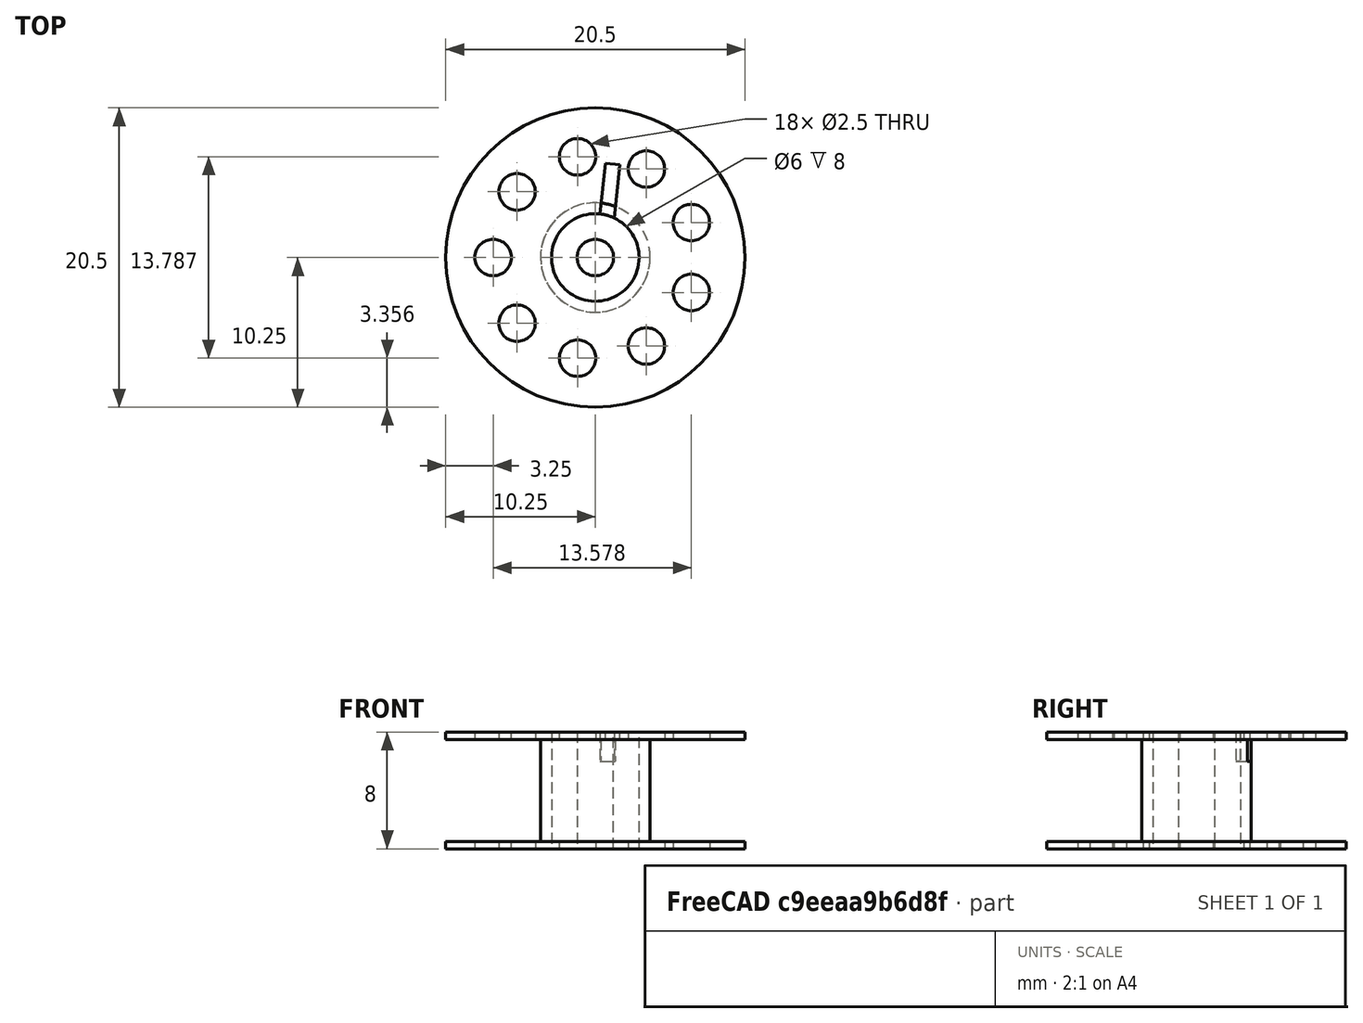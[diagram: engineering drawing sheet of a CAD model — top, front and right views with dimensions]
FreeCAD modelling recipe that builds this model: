
FCSTD DOCUMENT  (FreeCAD 0.21R33668 +7 (Git))
Label: Rast Gasser ZZ56
License: All rights reserved
LicenseURL: https://en.wikipedia.org/wiki/All_rights_reserved
objects: Part::Cylinder×5, Part::Cut×5, Part::FeaturePython×1, Part::Box×1
note: 11 computed .brp shape members not serialized (recipe doc carries the construction recipe); baked Part::Feature solids carry a one-line shape summary decoded from their .brp

FEATURE [Part::Cylinder] Cylinder
  Angle = 360
  AttacherType = Attacher::AttachEngine3D
  FirstAngle = 0
  Height = 8
  Radius = 10.25
  SecondAngle = 0
FEATURE [Part::Cylinder] Cylinder001
  Angle = 360
  AttacherType = Attacher::AttachEngine3D
  FirstAngle = 0
  Height = 8
  Radius = 3
  SecondAngle = 0
FEATURE [Part::Cut] Cut
  Base = -> Cylinder
  Tool = -> Cylinder001
FEATURE [Part::Cylinder] Cylinder002
  Angle = 360
  AttacherType = Attacher::AttachEngine3D
  FirstAngle = 0
  Height = 7
  Placement = pos=(0,0,0.5) rot=(0,0,1;0rad)
  Radius = 10.25
  SecondAngle = 0
FEATURE [Part::Cylinder] Cylinder003
  Angle = 360
  AttacherType = Attacher::AttachEngine3D
  FirstAngle = 0
  Height = 7
  Placement = pos=(0,0,0.5) rot=(0,0,1;0rad)
  Radius = 3.75
  SecondAngle = 0
FEATURE [Part::Cut] Cut001
  Base = -> Cylinder002
  Tool = -> Cylinder003
FEATURE [Part::Cut] Cut002
  Base = -> Cut
  Tool = -> Cut001
FEATURE [Part::Cylinder] Cylinder004
  Angle = 360
  AttacherType = Attacher::AttachEngine3D
  FirstAngle = 0
  Height = 8
  Radius = 1.25
  SecondAngle = 0
FEATURE [Part::FeaturePython] Array  # Draft array (typed FeaturePython)
  AlwaysSyncPlacement = false
  Angle = 360
  ArrayType = 2
  Axis = (0,0,1)
  Base = -> Cylinder004
  Center = (0,0,0)
  Count = 10
  ExpandArray = false
  Fuse = false
  IntervalAxis = (0,0,0)
  IntervalX = (50,0,0)
  IntervalY = (0,50,0)
  IntervalZ = (0,0,50)
  NumberCircles = 2
  NumberPolar = 5
  NumberX = 2
  NumberY = 2
  NumberZ = 1
  PlacementList = 10 placements: [(0,0,0),(-7,0,0),(-5.36231,-4.49951,0),(-1.21554,-6.89365,0),(3.5,-6.06218,0),(6.57785,-2.39414,0),(6.57785,2.39414,0),(3.5,6.06218,0),(-1.21554,6.89365,0),(-5.36231,4.49951,0)]
  RadialDistance = 7
  ScaleList = (10) [(1,1,1),(1,1,1),(1,1,1),(1,1,1),(1,1,1),(1,1,1),(1,1,1),(1,1,1),(1,1,1),(1,1,1)]
  Symmetry = 1
  TangentialDistance = 4.4
FEATURE [Part::Cut] Cut003
  Base = -> Cut002
  Tool = -> Array
FEATURE [Part::Box] Box  label="Cube"
  AttacherType = Attacher::AttachEngine3D
  Height = 2
  Length = 1
  Placement = pos=(0,0,6) rot=(0,0,-1;0.10472rad)
  Width = 6.5
FEATURE [Part::Cut] Cut004  label="Shuttle Coil"
  Base = -> Cut003
  Tool = -> Box
